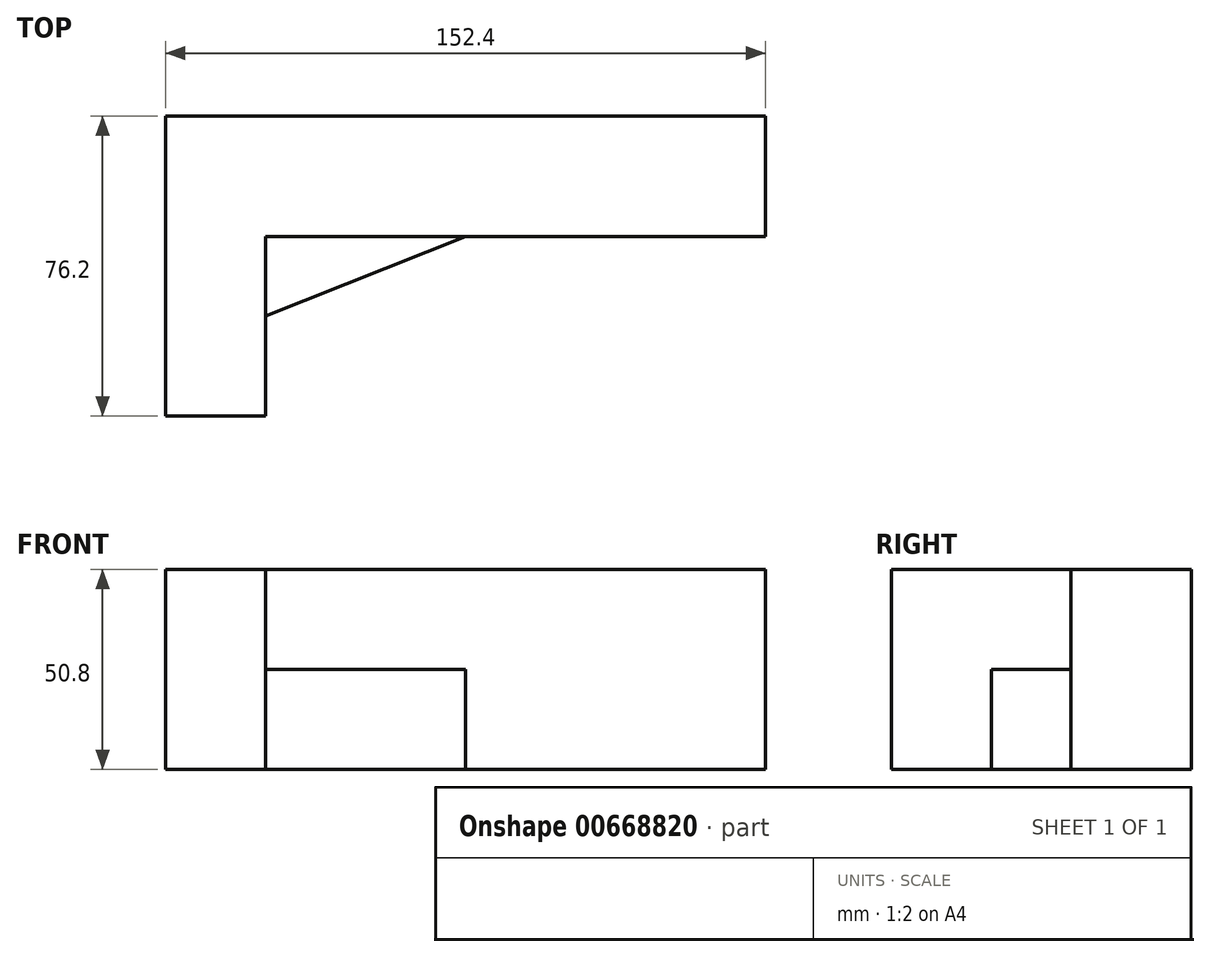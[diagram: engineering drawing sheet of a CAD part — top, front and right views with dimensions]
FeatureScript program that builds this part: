
annotation { "Feature Type Name" : "Feature", "Feature Type Description" : "" }
export const myFeature = defineFeature(function(context is Context, id is Id, definition is map)
    precondition{}
    {
        {
            var Q0;
            Q0=qCreatedBy(makeId("Top.planeOp"),FACE);
            var sketch = newSketch(context, id + "F0", { "sketchPlane" : qUnion([Q0])});
            skLineSegment(sketch, "E0", {"start": v(-65.51, 50.8) * mm, "end": v(86.89, 50.8) * mm});
            skLineSegment(sketch, "E1", {"start": v(-65.51, 50.8) * mm, "end": v(-65.51, -25.4) * mm});
            skLineSegment(sketch, "E2", {"start": v(-65.51, -25.4) * mm, "end": v(-40.11, -25.4) * mm});
            skLineSegment(sketch, "E3", {"start": v(-40.11, -25.4) * mm, "end": v(-40.11, 20.26) * mm});
            skLineSegment(sketch, "E4", {"start": v(-40.11, 20.26) * mm, "end": v(86.89, 20.26) * mm});
            skLineSegment(sketch, "E5", {"start": v(86.89, 20.26) * mm, "end": v(86.89, 50.8) * mm});
            skLineSegment(sketch, "E6", {"start": v(-40.11, 0) * mm, "end": v(10.69, 20.26) * mm});
            skSolve(sketch);
        }
        {
            var Q0;
            {var subQ3=sQuery(id+"F0.wireOp",EDGE,"E6");Q0=makeQuery(id+"F0.imprint","IMPRINT",FACE,{"disambiguationData":[TD([[makeQuery(id+"F0.imprint","IMPRINT",EDGE,{"derivedFrom":subQ3}),1.0]])]});}
            extrude(context, id + "F1", {"entities" : qUnion([Q0]), "depth" : 25.4 * mm, "offsetDistance" : 25.4 * mm});
        }
        {
            var Q0;
            Q0=makeQuery(id+"F0.imprint","IMPRINT",FACE,{"disambiguationData":[TD([[makeQuery(id+"F0.imprint","IMPRINT",EDGE,{"derivedFrom":sQuery(id+"F0.wireOp",EDGE,"E0")}),-1.0]])]});
            extrude(context, id + "F2", {"entities" : qUnion([Q0]), "depth" : 50.8 * mm, "offsetDistance" : 25.4 * mm});
        }
    });
